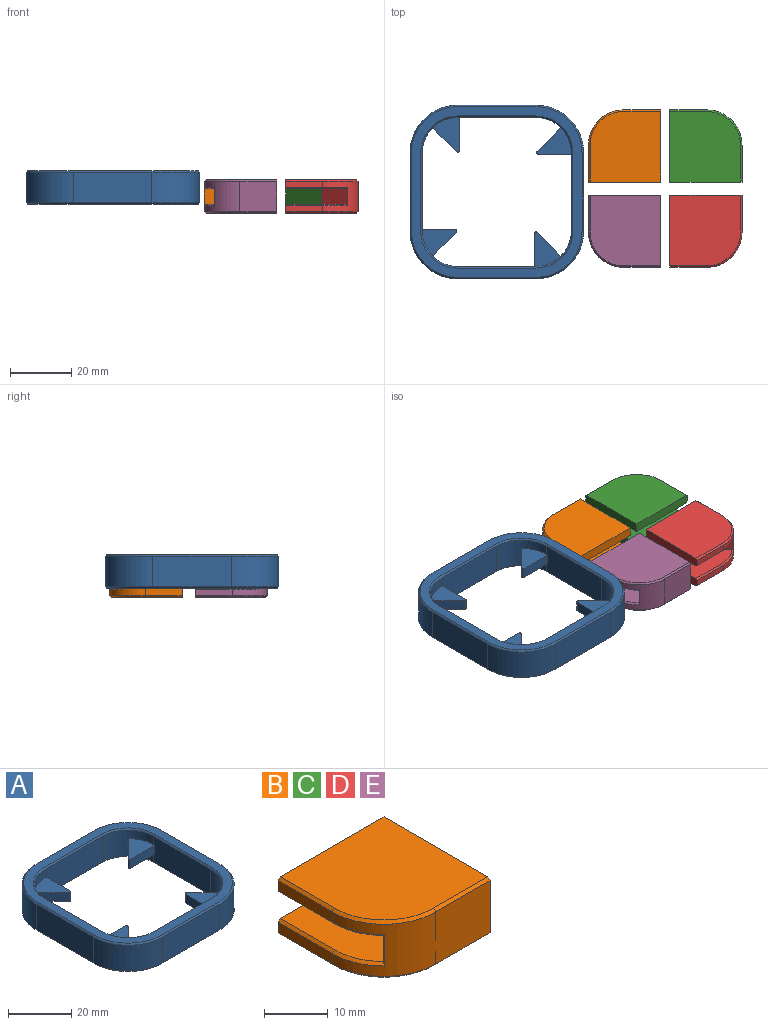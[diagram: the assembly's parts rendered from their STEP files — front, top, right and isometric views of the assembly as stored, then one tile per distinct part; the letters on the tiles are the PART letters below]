
ASSEMBLY  parts=5 mates=7
PART A: 70 faces, bbox 56.5x56.5x11 mm
  f0: plane 25.5x10mm, normal (-1,0,0), area 253.3mm2, adj f10,f11,f27,f28,f29,f34,f42
  f1: plane 25.5x10mm, normal (1,0,0), area 253.3mm2, adj f12,f13,f23,f24,f25,f41,f49
  f2: plane 25.5x10mm, normal (0,1,0), area 253.3mm2, adj f11,f12,f19,f20,f21,f38,f46
  f3: plane 25.5x10mm, normal (0,-1,0), area 253.3mm2, adj f10,f13,f15,f16,f17,f37,f45
  f4: plane 25.5x10mm, normal (-1,0,0), area 255mm2, adj f30,f33,f53,f61
  f5: plane 25.5x10mm, normal (0,-1,0), area 255mm2, adj f30,f31,f57,f65
  f6: plane 25.5x10mm, normal (1,0,0), area 255mm2, adj f31,f32,f54,f62
  f7: plane 25.5x10mm, normal (0,1,0), area 255mm2, adj f32,f33,f50,f58
  f8: plane 55.5x55.5mm, normal (0,0,1), area 560.5mm2, adj f42,f43,f44,f45,f46,f47,f48,f49
  f9: plane 55.5x55.5mm, normal (0,0,-1), area 560.5mm2, adj f34,f35,f36,f37,f38,f39,f40,f41
  f10: cylinder r=11.5mm len=11.5mm, axis (0,0,1), area 149.9mm2, adj f0,f3,f26,f27,f28,f35,f43
  f11: cylinder r=11.5mm len=11.5mm, axis (0,0,-1), area 149.9mm2, adj f0,f2,f18,f19,f20,f36,f44
  f12: cylinder r=11.5mm len=11.5mm, axis (0,0,1), area 149.9mm2, adj f1,f2,f22,f23,f24,f40,f48
  f13: cylinder r=11.5mm len=11.5mm, axis (0,0,-1), area 149.9mm2, adj f1,f3,f14,f15,f16,f39,f47
  f14: plane 7.78x7.78mm, normal (-0.71,-0.71,0), area 37.4mm2, adj f13,f15,f16,f69
  f15: plane 11.29x8.63mm, normal (0,0,1), area 57.5mm2, adj f3,f13,f14,f17,f69
  f16: plane 11.29x8.63mm, normal (0,0,-1), area 57.5mm2, adj f3,f13,f14,f17,f69
  f17: plane 10.79x3.4mm, normal (1,0,0), area 36.7mm2, adj f3,f15,f16,f69
  f18: plane 7.78x7.78mm, normal (0.71,0.71,0), area 37.4mm2, adj f11,f19,f20,f67
  f19: plane 11.29x8.63mm, normal (0,0,1), area 57.5mm2, adj f2,f11,f18,f21,f67
  f20: plane 11.29x8.63mm, normal (0,0,-1), area 57.5mm2, adj f2,f11,f18,f21,f67
  f21: plane 10.79x3.4mm, normal (-1,0,0), area 36.7mm2, adj f2,f19,f20,f67
  f22: plane 7.78x7.78mm, normal (0.71,-0.71,0), area 37.4mm2, adj f12,f23,f24,f68
  f23: plane 11.29x8.63mm, normal (0,0,1), area 57.5mm2, adj f1,f12,f22,f25,f68
  f24: plane 11.29x8.63mm, normal (0,0,-1), area 57.5mm2, adj f1,f12,f22,f25,f68
  f25: plane 10.79x3.4mm, normal (0,1,0), area 36.7mm2, adj f1,f23,f24,f68
  f26: plane 7.78x7.78mm, normal (-0.71,0.71,0), area 37.4mm2, adj f10,f27,f28,f66
  f27: plane 11.29x8.63mm, normal (0,0,1), area 57.5mm2, adj f0,f10,f26,f29,f66
  f28: plane 11.29x8.63mm, normal (0,0,-1), area 57.5mm2, adj f0,f10,f26,f29,f66
  f29: plane 10.79x3.4mm, normal (0,-1,0), area 36.7mm2, adj f0,f27,f28,f66
  f30: cylinder r=15.5mm len=15.5mm, axis (0,0,-1), area 243.5mm2, adj f4,f5,f55,f63
  f31: cylinder r=15.5mm len=15.5mm, axis (0,0,1), area 243.5mm2, adj f5,f6,f56,f64
  f32: cylinder r=15.5mm len=15.5mm, axis (0,0,-1), area 243.5mm2, adj f6,f7,f52,f60
  f33: cylinder r=15.5mm len=15.5mm, axis (0,0,1), area 243.5mm2, adj f4,f7,f51,f59
  f34: plane 25.5x0.5mm, normal (-0.71,0,-0.71), area 18mm2, adj f0,f9,f35,f36
  f35: cone r=12mm half-angle=45deg, axis (0,0,-1), area 13.1mm2, adj f9,f10,f34,f37
  f36: cone r=12mm half-angle=45deg, axis (0,0,-1), area 13.1mm2, adj f9,f11,f34,f38
  f37: plane 25.5x0.5mm, normal (0,-0.71,-0.71), area 18mm2, adj f3,f9,f35,f39
  f38: plane 25.5x0.5mm, normal (0,0.71,-0.71), area 18mm2, adj f2,f9,f36,f40
  f39: cone r=12mm half-angle=45deg, axis (0,0,-1), area 13.1mm2, adj f9,f13,f37,f41
  f40: cone r=12mm half-angle=45deg, axis (0,0,-1), area 13.1mm2, adj f9,f12,f38,f41
  f41: plane 25.5x0.5mm, normal (0.71,0,-0.71), area 18mm2, adj f1,f9,f39,f40
  f42: plane 25.5x0.5mm, normal (-0.71,0,0.71), area 18mm2, adj f0,f8,f43,f44
  f43: cone r=12mm half-angle=45deg, axis (0,0,1), area 13.1mm2, adj f8,f10,f42,f45
  f44: cone r=12mm half-angle=45deg, axis (0,0,1), area 13.1mm2, adj f8,f11,f42,f46
  f45: plane 25.5x0.5mm, normal (0,-0.71,0.71), area 18mm2, adj f3,f8,f43,f47
  f46: plane 25.5x0.5mm, normal (0,0.71,0.71), area 18mm2, adj f2,f8,f44,f48
  f47: cone r=12mm half-angle=45deg, axis (0,0,1), area 13.1mm2, adj f8,f13,f45,f49
  f48: cone r=12mm half-angle=45deg, axis (0,0,1), area 13.1mm2, adj f8,f12,f46,f49
  f49: plane 25.5x0.5mm, normal (0.71,0,0.71), area 18mm2, adj f1,f8,f47,f48
  f50: plane 25.5x0.5mm, normal (0,0.71,-0.71), area 18mm2, adj f7,f9,f51,f52
  f51: cone r=15mm half-angle=45deg, axis (0,0,1), area 16.9mm2, adj f9,f33,f50,f53
  f52: cone r=15mm half-angle=45deg, axis (0,0,1), area 16.9mm2, adj f9,f32,f50,f54
  f53: plane 25.5x0.5mm, normal (-0.71,0,-0.71), area 18mm2, adj f4,f9,f51,f55
  f54: plane 25.5x0.5mm, normal (0.71,0,-0.71), area 18mm2, adj f6,f9,f52,f56
  f55: cone r=15mm half-angle=45deg, axis (0,0,1), area 16.9mm2, adj f9,f30,f53,f57
  f56: cone r=15mm half-angle=45deg, axis (0,0,1), area 16.9mm2, adj f9,f31,f54,f57
  f57: plane 25.5x0.5mm, normal (0,-0.71,-0.71), area 18mm2, adj f5,f9,f55,f56
  f58: plane 25.5x0.5mm, normal (0,0.71,0.71), area 18mm2, adj f7,f8,f59,f60
  f59: cone r=15mm half-angle=45deg, axis (0,0,-1), area 16.9mm2, adj f8,f33,f58,f61
  f60: cone r=15mm half-angle=45deg, axis (0,0,-1), area 16.9mm2, adj f8,f32,f58,f62
  f61: plane 25.5x0.5mm, normal (-0.71,0,0.71), area 18mm2, adj f4,f8,f59,f63
  f62: plane 25.5x0.5mm, normal (0.71,0,0.71), area 18mm2, adj f6,f8,f60,f64
  f63: cone r=15mm half-angle=45deg, axis (0,0,-1), area 16.9mm2, adj f8,f30,f61,f65
  f64: cone r=15mm half-angle=45deg, axis (0,0,-1), area 16.9mm2, adj f8,f31,f62,f65
  f65: plane 25.5x0.5mm, normal (0,-0.71,0.71), area 18mm2, adj f5,f8,f63,f64
  f66: cylinder r=0.5mm len=3.4mm, axis (0,0,1), area 4mm2, adj f26,f27,f28,f29
  f67: cylinder r=0.5mm len=3.4mm, axis (0,0,1), area 4mm2, adj f18,f19,f20,f21
  f68: cylinder r=0.5mm len=3.4mm, axis (0,0,1), area 4mm2, adj f22,f23,f24,f25
  f69: cylinder r=0.5mm len=3.4mm, axis (0,0,1), area 4mm2, adj f14,f15,f16,f17
PART B: 24 faces, bbox 23.5x23.5x11 mm
  f0: plane 12x10mm, normal (0,-1,0), area 120mm2, adj f1,f6,f8,f13,f16,f19
  f1: plane 23.5x3mm, normal (1,0,0), area 70.4mm2, adj f0,f2,f4,f5,f19
  f2: plane 23.5x3mm, normal (0,1,0), area 70.2mm2, adj f1,f3,f4,f5,f17,f22
  f3: plane 12x2mm, normal (-1,0,0), area 24mm2, adj f2,f13,f17,f22
  f4: plane 23x23mm, normal (0,0,1), area 503mm2, adj f1,f2,f17,f18,f19
  f5: plane 23.5x23mm, normal (0,0,-1), area 389.6mm2, adj f1,f2,f6,f7,f22,f23
  f6: plane 11.75x11.75mm, normal (0.71,0.71,0), area 83.1mm2, adj f0,f5,f7,f12
  f7: plane 8.38x8.38mm, normal (-0.71,0.71,0), area 59.5mm2, adj f5,f6,f12,f13,f21,f23
  f8: plane 23.5x3mm, normal (1,0,0), area 70.4mm2, adj f0,f9,f11,f12,f16
  f9: plane 23.5x3mm, normal (0,1,0), area 70.2mm2, adj f8,f10,f11,f12,f14,f20
  f10: plane 12x2mm, normal (-1,0,0), area 24mm2, adj f9,f13,f14,f20
  f11: plane 23x23mm, normal (0,0,-1), area 503mm2, adj f8,f9,f14,f15,f16
  f12: plane 23.5x23mm, normal (0,0,1), area 389.6mm2, adj f6,f7,f8,f9,f20,f21
  f13: cylinder r=11.5mm len=11.5mm, axis (0,0,-1), area 126.4mm2, adj f0,f3,f7,f10,f15,f18,f21,f23
  f14: plane 12x0.5mm, normal (-0.71,0,-0.71), area 8.5mm2, adj f9,f10,f11,f15
  f15: cone r=11mm half-angle=45deg, axis (0,0,1), area 12.5mm2, adj f11,f13,f14,f16
  f16: plane 12x0.5mm, normal (0,-0.71,-0.71), area 8.5mm2, adj f0,f8,f11,f15
  f17: plane 12x0.5mm, normal (-0.71,0,0.71), area 8.5mm2, adj f2,f3,f4,f18
  f18: cone r=11mm half-angle=45deg, axis (0,0,-1), area 12.5mm2, adj f4,f13,f17,f19
  f19: plane 12x0.5mm, normal (0,-0.71,0.71), area 8.5mm2, adj f0,f1,f4,f18
  f20: plane 12x0.5mm, normal (-0.71,0,0.71), area 8.5mm2, adj f9,f10,f12,f21
  f21: cone r=11mm half-angle=45deg, axis (0,0,-1), area 6.2mm2, adj f7,f12,f13,f20
  f22: plane 12x0.5mm, normal (-0.71,0,-0.71), area 8.5mm2, adj f2,f3,f5,f23
  f23: cone r=11mm half-angle=45deg, axis (0,0,1), area 6.2mm2, adj f5,f7,f13,f22
PART C: same geometry as B
PART D: same geometry as B
PART E: same geometry as B
PLACE A t=(-12.3,2.95,9.58)mm fixed
PLACE B rot(axis=(0,0,-1),90deg) t=(41.05,29.68,9.11)mm
PLACE C rot(axis=(0,0,1),180deg) t=(67.52,6.18,9.11)mm
PLACE D rot(axis=(0,0,1),90deg) t=(44.02,-21.58,9.11)mm
PLACE E rot(axis=(0,0,1),0deg) t=(17.55,1.92,9.11)mm
MATE planar E.f3 <-> B.f0  axis (-1,0,0) through (17.55,-4.08,10.61)mm
MATE planar E.f11 <-> C.f11  axis (0,0,-1) through (30.02,-9.12,1.11)mm
MATE parallel A.f15 <-> B.f4  axis (0,0,1) through (-27.61,22.51,11.28)mm
MATE planar E.f4 <-> B.f4  axis (0,0,1) through (30.02,-9.12,12.11)mm
MATE planar E.f4 <-> D.f4  axis (0,0,1) through (30.02,-9.12,12.11)mm
MATE planar D.f0 <-> C.f3  axis (1,0,0) through (67.52,-4.08,6.61)mm
MATE planar B.f3 <-> C.f0  axis (0,1,0) through (35.05,29.68,10.61)mm
